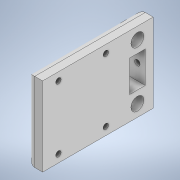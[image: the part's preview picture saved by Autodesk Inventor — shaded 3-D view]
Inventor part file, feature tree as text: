
AUTODESK INVENTOR PART (.ipt)
format: ipt  version: 2022.3 (Build 263350000, 350)  size: 207,872 bytes
history: native  units: mm
features: sketch x5, extrude x3, hole x3, fillet x1
ambient origin geometry x8: Origin, YZ Plane, XZ Plane, XY Plane, X Axis, Y Axis, Z Axis, Center Point
bodies: Solid1 (feature_tree)
feature tree (12):
  extrude  "Extrusion1"  Depth=10.0mm
  sketch  "Sketch2"  dims[d2=50.0mm d3=0.0mm d4=20.0mm]
  extrude  "Extrusion2"  Depth=20.0mm
  extrude  "Extrusion3"  Depth=7.5mm
  hole  "Hole1"  [1 undecoded]
  sketch  "Sketch4"  dims[d7=90.0deg d8=8.2mm d9=12.0mm]
  fillet  "Fillet1"  Radius=12.0mm
  hole  "Hole2"  [1 undecoded]
  hole  "Hole3"  [1 undecoded]
  sketch  "Sketch1"  dims[d0=10.0mm d1=70.0mm]
  sketch  "Sketch3"  dims[d5=7.5mm d6=7.5mm]
  sketch  "Sketch5"  dims[d10=8.2mm d11=12.0mm d12=10.0mm d13=20.0mm d14=0.0mm d15=0.0mm d16=2.0mm d17=0.0mm d18=10.0mm d19=5.0mm d20=30.0mm d21=40.0mm d22=3.4mm d23=6.0mm d24=5.9mm d25=2.0mm d26=90.0deg d27=1.2mm d28=0.0mm d29=5.0mm d30=5.0mm d31=90.0deg d32=3.4mm d33=6.0mm d34=5.9mm d35=2.0mm d36=90.0deg d37=5.0mm d38=0.0mm d39=3.4mm d40=6.0mm d41=4.1mm d42=5.1mm d43=90.0deg d44=6.9mm d45=0.0mm]
note: 3 required parameter values undecoded (feature->parameter linkage not recoverable at this tier; creation-order binding heuristic only, values carry confidence <= 0.55)
